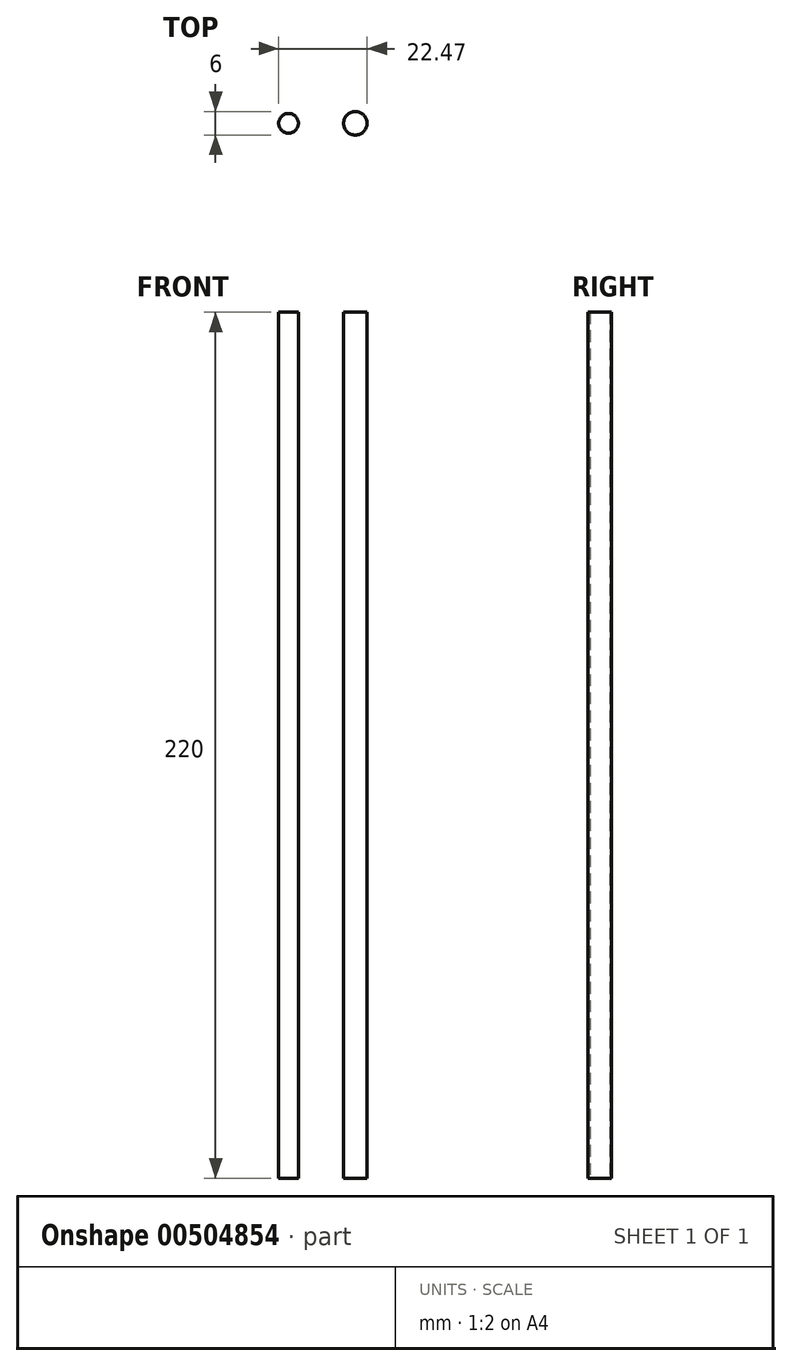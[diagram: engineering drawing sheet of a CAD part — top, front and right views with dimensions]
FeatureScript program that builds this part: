
annotation { "Feature Type Name" : "Feature", "Feature Type Description" : "" }
export const myFeature = defineFeature(function(context is Context, id is Id, definition is map)
    precondition{}
    {
        {
            var Q0;
            Q0=qCreatedBy(makeId("Top.planeOp"),FACE);
            var sketch = newSketch(context, id + "F0", { "sketchPlane" : qUnion([Q0])});
            skCircle(sketch, "E0", {"center": v(0, 0) * mm, "radius": 2.5 * mm});
            skCircle(sketch, "E1", {"center": v(16.97, 0) * mm, "radius": 3 * mm});
            skSolve(sketch);
        }
        {
            var Q0;
            Q0=qSketchRegion(id+"F0",true);
            extrude(context, id + "F1", {"entities" : qUnion([Q0]), "depth" : 220 * mm});
        }
    });
